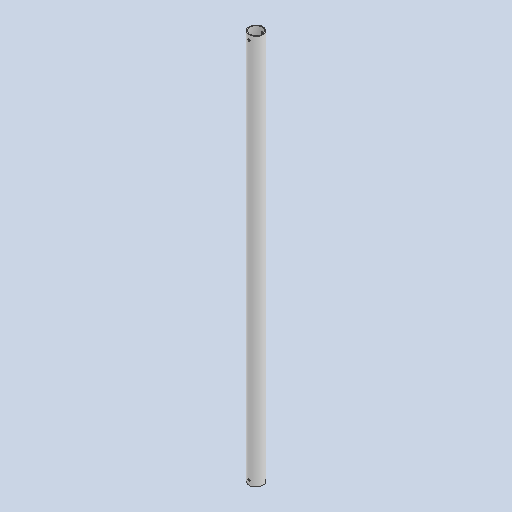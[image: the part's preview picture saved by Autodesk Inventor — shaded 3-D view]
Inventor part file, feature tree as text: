
AUTODESK INVENTOR PART (.ipt)
format: ipt  version: 2022 (Build 260153000, 153)  size: 175,104 bytes
history: native  units: mm
features: extrude x2, sketch x2
ambient origin geometry x8: Origin, YZ Plane, XZ Plane, XY Plane, X Axis, Y Axis, Z Axis, Center Point
bodies: Body1 (feature_tree)
feature tree (4):
  extrude  "Extrusion5"  Depth=18.0mm
  extrude  "Extrusion6"  Depth=10.0mm TaperAngle=0.0deg
  sketch  "Sketch2"  dims[d31=34.456mm d91=18.0mm]
  sketch  "Sketch3"  dims[d92=16.0mm d93=500.0mm d94=0.0mm d95=6.0mm d96=3.0mm d97=6.0mm d98=3.0mm d99=10.0mm d100=10.0mm d101=0.0mm d102=0.0mm]
